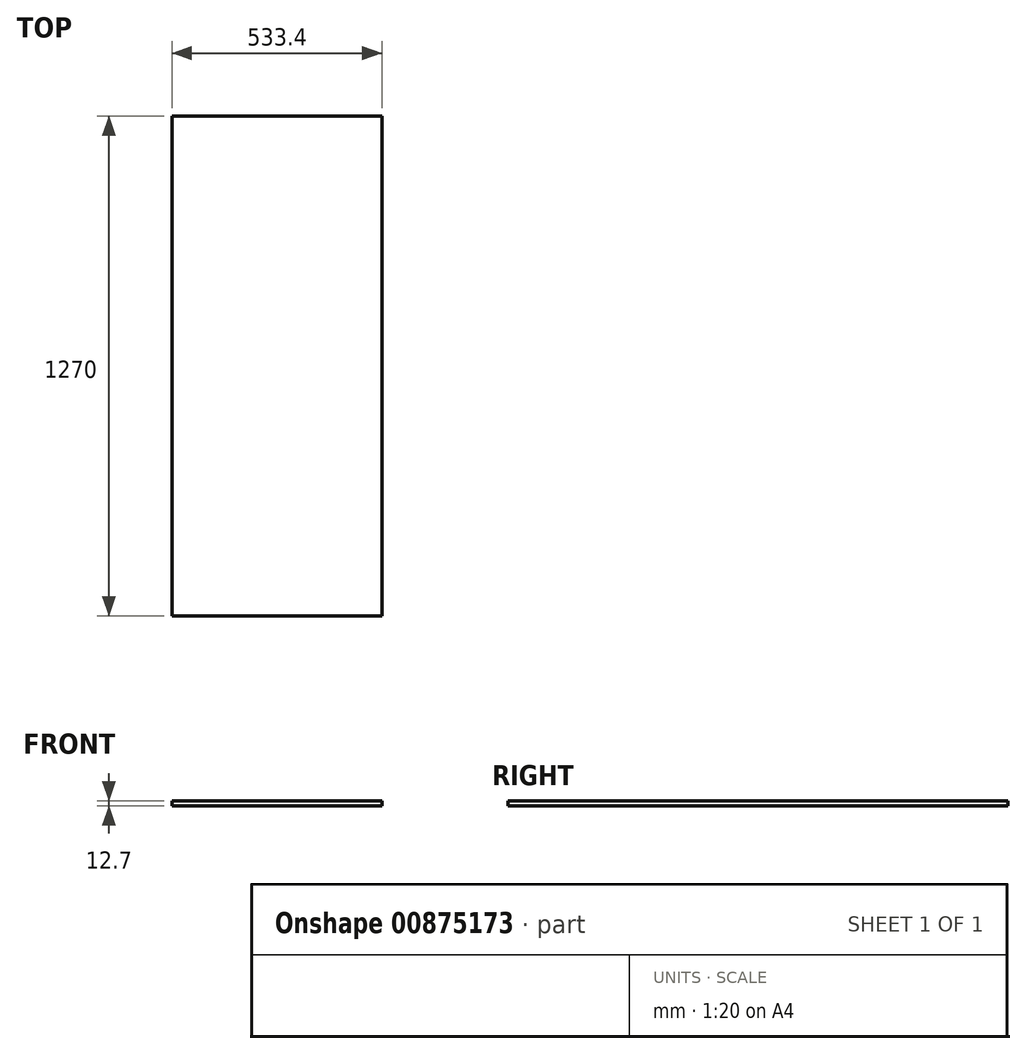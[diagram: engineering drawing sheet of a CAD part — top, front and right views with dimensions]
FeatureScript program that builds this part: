
annotation { "Feature Type Name" : "Feature", "Feature Type Description" : "" }
export const myFeature = defineFeature(function(context is Context, id is Id, definition is map)
    precondition{}
    {
        {
            var Q0;
            Q0=qCreatedBy(makeId("Front.planeOp"),FACE);
            var sketch = newSketch(context, id + "F0", { "sketchPlane" : qUnion([Q0])});
            skLineSegment(sketch, "E0.bottom", {"start": v(-614.68, -4.66) * mm, "end": v(-81.28, -4.66) * mm});
            skLineSegment(sketch, "E0.top", {"start": v(-614.68, -17.36) * mm, "end": v(-81.28, -17.36) * mm});
            skLineSegment(sketch, "E0.left", {"start": v(-614.68, -4.66) * mm, "end": v(-614.68, -17.36) * mm});
            skLineSegment(sketch, "E0.right", {"start": v(-81.28, -4.66) * mm, "end": v(-81.28, -17.36) * mm});
            skSolve(sketch);
        }
        {
            var Q0;
            Q0=makeQuery(id+"F0.imprint","IMPRINT",FACE,{"disambiguationData":[TD([[makeQuery(id+"F0.imprint","IMPRINT",EDGE,{"derivedFrom":sQuery(id+"F0.wireOp",EDGE,"E0.bottom")}),-1.0]])]});
            extrude(context, id + "F1", {"entities" : qUnion([Q0]), "depth" : 1270 * mm, "offsetDistance" : 25.4 * mm});
        }
    });
